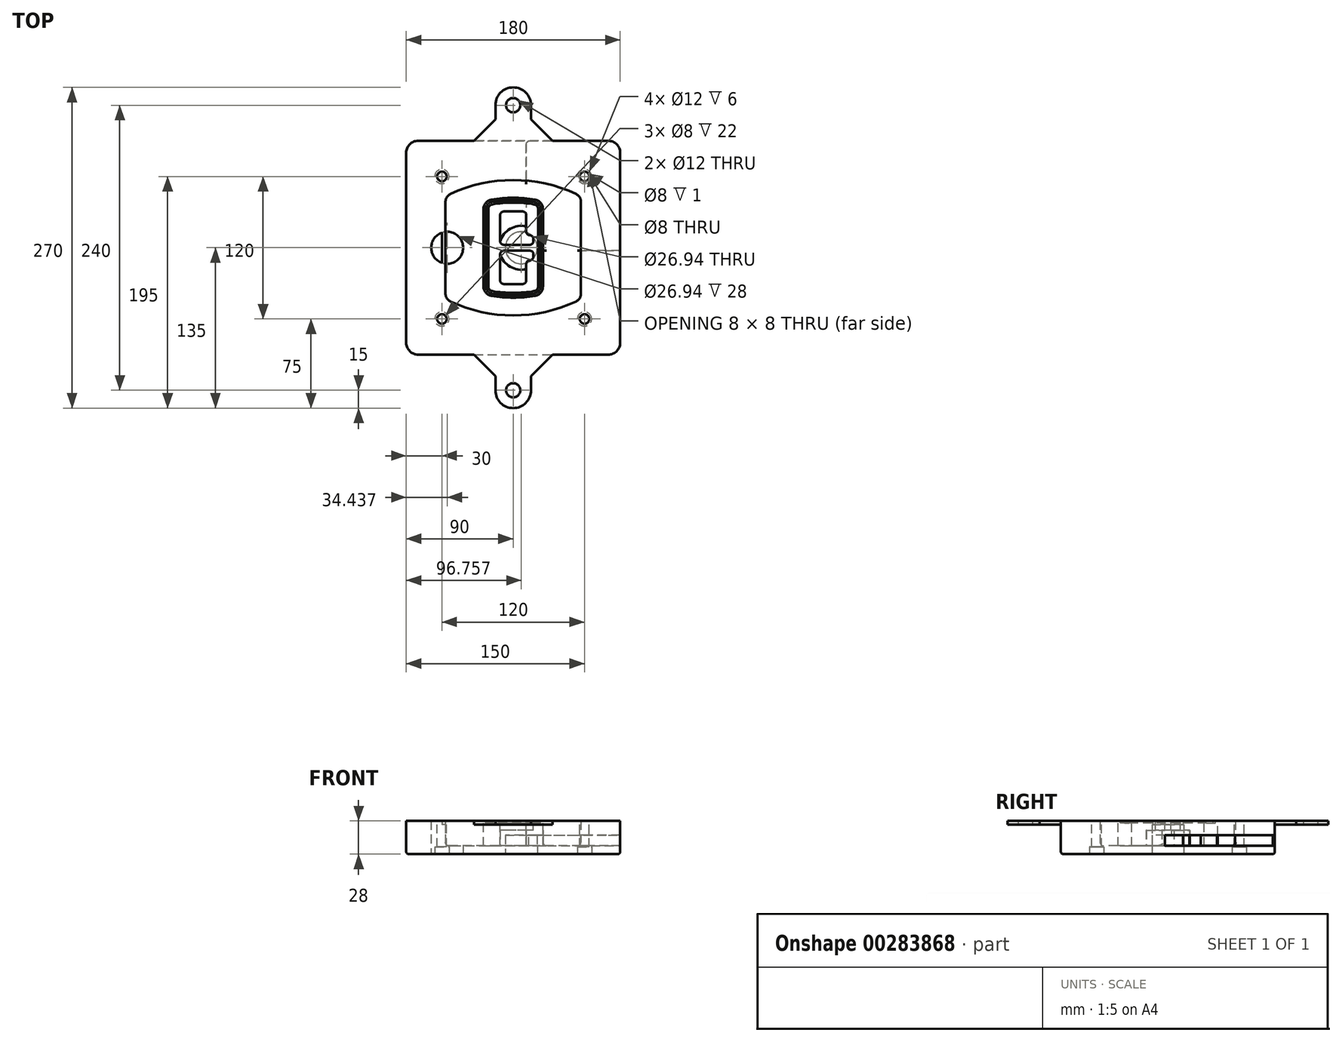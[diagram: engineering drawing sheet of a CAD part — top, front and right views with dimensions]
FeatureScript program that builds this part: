
annotation { "Feature Type Name" : "Feature", "Feature Type Description" : "" }
export const myFeature = defineFeature(function(context is Context, id is Id, definition is map)
    precondition{}
    {
        {
            var Q0;
            Q0=qCreatedBy(makeId("Top.planeOp"),FACE);
            var sketch = newSketch(context, id + "F0", { "sketchPlane" : qUnion([Q0])});
            skPoint(sketch, "E0.rect.middle", {"position": v(0, 0) * mm});
            skLineSegment(sketch, "E1.bottom", {"start": v(-80, -90) * mm, "end": v(80, -90) * mm});
            skLineSegment(sketch, "E1.top", {"start": v(-80, 90) * mm, "end": v(80, 90) * mm});
            skLineSegment(sketch, "E1.left", {"start": v(-90, -80) * mm, "end": v(-90, 80) * mm});
            skLineSegment(sketch, "E1.right", {"start": v(90, -80) * mm, "end": v(90, 80) * mm});
            skLineSegment(sketch, "E2", {"start": v(-90, 90) * mm, "end": v(90, -90) * mm, "construction": true});
            skLineSegment(sketch, "E3", {"start": v(90, 90) * mm, "end": v(-90, -90) * mm, "construction": true});
            skCircle(sketch, "E4", {"center": v(-60, 60) * mm, "radius": 4 * mm});
            skCircle(sketch, "E5", {"center": v(60, 60) * mm, "radius": 4 * mm});
            skCircle(sketch, "E6", {"center": v(60, -60) * mm, "radius": 4 * mm});
            skCircle(sketch, "E7", {"center": v(-60, -60) * mm, "radius": 4 * mm});
            skLineSegment(sketch, "E8", {"start": v(-60, 60) * mm, "end": v(60, 60) * mm, "construction": true});
            skLineSegment(sketch, "E9", {"start": v(60, 60) * mm, "end": v(60, -60) * mm, "construction": true});
            skLineSegment(sketch, "E10", {"start": v(60, -60) * mm, "end": v(-60, -60) * mm, "construction": true});
            skLineSegment(sketch, "E11", {"start": v(-60, -60) * mm, "end": v(-60, 60) * mm, "construction": true});
            skLineSegment(sketch, "E12", {"start": v(-60, 38.83) * mm, "end": v(-60, -38.83) * mm});
            skLineSegment(sketch, "E13", {"start": v(60, 38.83) * mm, "end": v(60, -38.83) * mm});
            skArc(sketch, "E14", {"start": v(54.26, 47.88) * mm, "mid": v(0, 60) * mm, "end": v(-54.26, 47.88) * mm});
            skArc(sketch, "E15", {"start": v(-54.26, -47.88) * mm, "mid": v(0, -60) * mm, "end": v(54.26, -47.88) * mm});
            skLineSegment(sketch, "E16", {"start": v(-60, 0) * mm, "end": v(60, 0) * mm, "construction": true});
            skPoint(sketch, "E17.visualSharp", {"position": v(-60, -45) * mm});
            skArc(sketch, "E17.filletArc", {"start": v(-60, -38.83) * mm, "mid": v(-58.44, -44.2) * mm, "end": v(-54.26, -47.88) * mm});
            skPoint(sketch, "E18.visualSharp", {"position": v(-60, 45) * mm});
            skArc(sketch, "E18.filletArc", {"start": v(-54.26, 47.88) * mm, "mid": v(-58.44, 44.2) * mm, "end": v(-60, 38.83) * mm});
            skPoint(sketch, "E19.visualSharp", {"position": v(60, 45) * mm});
            skArc(sketch, "E19.filletArc", {"start": v(60, 38.83) * mm, "mid": v(58.44, 44.2) * mm, "end": v(54.26, 47.88) * mm});
            skPoint(sketch, "E20.visualSharp", {"position": v(60, -45) * mm});
            skArc(sketch, "E20.filletArc", {"start": v(54.26, -47.88) * mm, "mid": v(58.44, -44.2) * mm, "end": v(60, -38.83) * mm});
            skPoint(sketch, "E21.visualSharp", {"position": v(-90, 90) * mm});
            skArc(sketch, "E21.filletArc", {"start": v(-80, 90) * mm, "mid": v(-87.07, 87.07) * mm, "end": v(-90, 80) * mm});
            skPoint(sketch, "E22.visualSharp", {"position": v(90, 90) * mm});
            skArc(sketch, "E22.filletArc", {"start": v(90, 80) * mm, "mid": v(87.07, 87.07) * mm, "end": v(80, 90) * mm});
            skPoint(sketch, "E23.visualSharp", {"position": v(90, -90) * mm});
            skArc(sketch, "E23.filletArc", {"start": v(80, -90) * mm, "mid": v(87.07, -87.07) * mm, "end": v(90, -80) * mm});
            skPoint(sketch, "E24.visualSharp", {"position": v(-90, -90) * mm});
            skArc(sketch, "E24.filletArc", {"start": v(-90, -80) * mm, "mid": v(-87.07, -87.07) * mm, "end": v(-80, -90) * mm});
            skArc(sketch, "E25.0", {"start": v(57, 38.83) * mm, "mid": v(55.9, 42.58) * mm, "end": v(52.98, 45.17) * mm});
            skLineSegment(sketch, "E25.1", {"start": v(57, 38.83) * mm, "end": v(57, -38.83) * mm});
            skArc(sketch, "E25.2", {"start": v(52.98, -45.17) * mm, "mid": v(55.9, -42.58) * mm, "end": v(57, -38.83) * mm});
            skArc(sketch, "E25.3", {"start": v(-52.98, -45.17) * mm, "mid": v(0, -57) * mm, "end": v(52.98, -45.17) * mm});
            skArc(sketch, "E25.4", {"start": v(-57, -38.83) * mm, "mid": v(-55.9, -42.58) * mm, "end": v(-52.98, -45.17) * mm});
            skArc(sketch, "E25.5", {"start": v(52.98, 45.17) * mm, "mid": v(0, 57) * mm, "end": v(-52.98, 45.17) * mm});
            skLineSegment(sketch, "E25.6", {"start": v(-57, 38.83) * mm, "end": v(-57, -38.83) * mm});
            skArc(sketch, "E25.7", {"start": v(-52.98, 45.17) * mm, "mid": v(-55.9, 42.58) * mm, "end": v(-57, 38.83) * mm});
            skArc(sketch, "E26.0", {"start": v(-55.96, 51.5) * mm, "mid": v(-61.82, 46.33) * mm, "end": v(-64, 38.83) * mm});
            skArc(sketch, "E26.1", {"start": v(55.96, 51.5) * mm, "mid": v(0, 64) * mm, "end": v(-55.96, 51.5) * mm});
            skArc(sketch, "E26.2", {"start": v(64, 38.83) * mm, "mid": v(61.82, 46.33) * mm, "end": v(55.96, 51.5) * mm});
            skLineSegment(sketch, "E26.3", {"start": v(64, 38.83) * mm, "end": v(64, -38.83) * mm});
            skArc(sketch, "E26.4", {"start": v(55.96, -51.5) * mm, "mid": v(61.82, -46.33) * mm, "end": v(64, -38.83) * mm});
            skLineSegment(sketch, "E26.5", {"start": v(-64, 38.83) * mm, "end": v(-64, -38.83) * mm});
            skArc(sketch, "E26.6", {"start": v(-55.96, -51.5) * mm, "mid": v(0, -64) * mm, "end": v(55.96, -51.5) * mm});
            skArc(sketch, "E26.7", {"start": v(-64, -38.83) * mm, "mid": v(-61.82, -46.33) * mm, "end": v(-55.96, -51.5) * mm});
            skSolve(sketch);
        }
        {
            var Q0;
            Q0=makeQuery(id+"F0.imprint","IMPRINT",FACE,{"disambiguationData":[TD([[makeQuery(id+"F0.imprint","IMPRINT",EDGE,{"derivedFrom":sQuery(id+"F0.wireOp",EDGE,"E1.bottom")}),1.0]])]});
            var Q1;
            Q1=makeQuery(id+"F0.imprint","IMPRINT",FACE,{"disambiguationData":[TD([[makeQuery(id+"F0.imprint","IMPRINT",EDGE,{"derivedFrom":sQuery(id+"F0.wireOp",EDGE,"E12")}),1.0]])]});
            var Q2;
            Q2=makeQuery(id+"F0.imprint","IMPRINT",FACE,{"disambiguationData":[TD([[makeQuery(id+"F0.imprint","IMPRINT",EDGE,{"derivedFrom":sQuery(id+"F0.wireOp",EDGE,"E25.0")}),1.0]])]});
            var Q3;
            Q3=makeQuery(id+"F0.imprint","IMPRINT",FACE,{"disambiguationData":[TD([[makeQuery(id+"F0.imprint","IMPRINT",EDGE,{"derivedFrom":sQuery(id+"F0.wireOp",EDGE,"E12")}),-1.0]])]});
            extrude(context, id + "F1", {"entities" : qUnion([Q0, Q1, Q2, Q3]), "oppositeDirection" : true, "depth" : 25 * mm});
        }
        {
            var Q0;
            Q0=makeQuery(id+"F0.imprint","IMPRINT",FACE,{"disambiguationData":[TD([[makeQuery(id+"F0.imprint","IMPRINT",EDGE,{"derivedFrom":sQuery(id+"F0.wireOp",EDGE,"E12")}),1.0]])]});
            extrude(context, id + "F2", {"entities" : qUnion([Q0]), "operationType" : NewBodyOperationType.ADD, "depth" : 3 * mm});
        }
        {
            var Q0;
            Q0=makeQuery(id+"F0.imprint","IMPRINT",FACE,{"disambiguationData":[TD([[makeQuery(id+"F0.imprint","IMPRINT",EDGE,{"derivedFrom":sQuery(id+"F0.wireOp",EDGE,"E25.0")}),1.0]])]});
            extrude(context, id + "F3", {"entities" : qUnion([Q0]), "operationType" : NewBodyOperationType.REMOVE, "oppositeDirection" : true, "depth" : 18 * mm});
        }
        {
            var Q0;
            Q0=makeQuery(id+"F2.opExtrude","CAP_FACE",FACE,{"disambiguationData":[OSD([sQuery(id+"F0.wireOp",EDGE,"E12"),sQuery(id+"F0.wireOp",EDGE,"E13"),sQuery(id+"F0.wireOp",EDGE,"E14"),sQuery(id+"F0.wireOp",EDGE,"E15"),sQuery(id+"F0.wireOp",EDGE,"E17.filletArc"),sQuery(id+"F0.wireOp",EDGE,"E18.filletArc"),sQuery(id+"F0.wireOp",EDGE,"E19.filletArc"),sQuery(id+"F0.wireOp",EDGE,"E20.filletArc"),sQuery(id+"F0.wireOp",EDGE,"E25.0"),sQuery(id+"F0.wireOp",EDGE,"E25.1"),sQuery(id+"F0.wireOp",EDGE,"E25.2"),sQuery(id+"F0.wireOp",EDGE,"E25.3"),sQuery(id+"F0.wireOp",EDGE,"E25.4"),sQuery(id+"F0.wireOp",EDGE,"E25.5"),sQuery(id+"F0.wireOp",EDGE,"E25.6"),sQuery(id+"F0.wireOp",EDGE,"E25.7")])],"isStart":false});
            var sketch = newSketch(context, id + "F4", { "sketchPlane" : qUnion([Q0])});
            skArc(sketch, "E27.0", {"start": v(-18.34, -40.45) * mm, "mid": v(0, -42) * mm, "end": v(18.34, -40.45) * mm});
            skArc(sketch, "E28.0", {"start": v(18.34, 40.45) * mm, "mid": v(0, 42) * mm, "end": v(-18.34, 40.45) * mm});
            skLineSegment(sketch, "E29", {"start": v(-25, 32.57) * mm, "end": v(-25, -32.57) * mm});
            skLineSegment(sketch, "E30", {"start": v(25, 32.57) * mm, "end": v(25, -32.57) * mm});
            skLineSegment(sketch, "E31", {"start": v(-25, 39.1) * mm, "end": v(25, 39.1) * mm, "construction": true});
            skLineSegment(sketch, "E32", {"start": v(-25, -39.1) * mm, "end": v(25, -39.1) * mm, "construction": true});
            skPoint(sketch, "E33.visualSharp", {"position": v(-25, 39.1) * mm});
            skArc(sketch, "E33.filletArc", {"start": v(-18.34, 40.45) * mm, "mid": v(-23.11, 37.73) * mm, "end": v(-25, 32.57) * mm});
            skPoint(sketch, "E34.visualSharp", {"position": v(25, 39.1) * mm});
            skArc(sketch, "E34.filletArc", {"start": v(25, 32.57) * mm, "mid": v(23.11, 37.73) * mm, "end": v(18.34, 40.45) * mm});
            skPoint(sketch, "E35.visualSharp", {"position": v(25, -39.1) * mm});
            skArc(sketch, "E35.filletArc", {"start": v(18.34, -40.45) * mm, "mid": v(23.11, -37.73) * mm, "end": v(25, -32.57) * mm});
            skPoint(sketch, "E36.visualSharp", {"position": v(-25, -39.1) * mm});
            skArc(sketch, "E36.filletArc", {"start": v(-25, -32.57) * mm, "mid": v(-23.11, -37.73) * mm, "end": v(-18.34, -40.45) * mm});
            skArc(sketch, "E37.0", {"start": v(52.98, 45.17) * mm, "mid": v(0, 57) * mm, "end": v(-52.98, 45.17) * mm});
            skArc(sketch, "E37.1", {"start": v(-52.98, 45.17) * mm, "mid": v(-55.9, 42.58) * mm, "end": v(-57, 38.83) * mm});
            skLineSegment(sketch, "E37.2", {"start": v(-57, 38.83) * mm, "end": v(-57, -38.83) * mm});
            skArc(sketch, "E37.3", {"start": v(-57, -38.83) * mm, "mid": v(-55.9, -42.58) * mm, "end": v(-52.98, -45.17) * mm});
            skArc(sketch, "E37.4", {"start": v(-52.98, -45.17) * mm, "mid": v(0, -57) * mm, "end": v(52.98, -45.17) * mm});
            skArc(sketch, "E37.5", {"start": v(52.98, -45.17) * mm, "mid": v(55.9, -42.58) * mm, "end": v(57, -38.83) * mm});
            skLineSegment(sketch, "E37.6", {"start": v(57, 38.83) * mm, "end": v(57, -38.83) * mm});
            skArc(sketch, "E37.7", {"start": v(57, 38.83) * mm, "mid": v(55.9, 42.58) * mm, "end": v(52.98, 45.17) * mm});
            skLineSegment(sketch, "E38.0", {"start": v(23, 32.57) * mm, "end": v(23, -32.57) * mm});
            skArc(sketch, "E38.1", {"start": v(18, -38.48) * mm, "mid": v(21.58, -36.44) * mm, "end": v(23, -32.57) * mm});
            skArc(sketch, "E38.2", {"start": v(-18, -38.48) * mm, "mid": v(0, -40) * mm, "end": v(18, -38.48) * mm});
            skArc(sketch, "E38.3", {"start": v(-23, -32.57) * mm, "mid": v(-21.58, -36.44) * mm, "end": v(-18, -38.48) * mm});
            skLineSegment(sketch, "E38.4", {"start": v(-23, 32.57) * mm, "end": v(-23, -32.57) * mm});
            skArc(sketch, "E38.5", {"start": v(23, 32.57) * mm, "mid": v(21.58, 36.44) * mm, "end": v(18, 38.48) * mm});
            skArc(sketch, "E38.6", {"start": v(-18, 38.48) * mm, "mid": v(-21.58, 36.44) * mm, "end": v(-23, 32.57) * mm});
            skArc(sketch, "E38.7", {"start": v(18, 38.48) * mm, "mid": v(0, 40) * mm, "end": v(-18, 38.48) * mm});
            skArc(sketch, "E39.0", {"start": v(21, 32.57) * mm, "mid": v(20.06, 35.15) * mm, "end": v(17.67, 36.5) * mm});
            skLineSegment(sketch, "E39.1", {"start": v(21, 32.57) * mm, "end": v(21, -32.57) * mm});
            skArc(sketch, "E39.2", {"start": v(17.67, -36.5) * mm, "mid": v(20.06, -35.15) * mm, "end": v(21, -32.57) * mm});
            skArc(sketch, "E39.3", {"start": v(-17.67, -36.5) * mm, "mid": v(0, -38) * mm, "end": v(17.67, -36.5) * mm});
            skArc(sketch, "E39.4", {"start": v(-21, -32.57) * mm, "mid": v(-20.06, -35.15) * mm, "end": v(-17.67, -36.5) * mm});
            skArc(sketch, "E39.5", {"start": v(17.67, 36.5) * mm, "mid": v(0, 38) * mm, "end": v(-17.67, 36.5) * mm});
            skLineSegment(sketch, "E39.6", {"start": v(-21, 32.57) * mm, "end": v(-21, -32.57) * mm});
            skArc(sketch, "E39.7", {"start": v(-17.67, 36.5) * mm, "mid": v(-20.06, 35.15) * mm, "end": v(-21, 32.57) * mm});
            skLineSegment(sketch, "E40", {"start": v(-25, 0) * mm, "end": v(25, 0) * mm, "construction": true});
            skLineSegment(sketch, "E41", {"start": v(-11, 5.5) * mm, "end": v(-11, 27.5) * mm});
            skLineSegment(sketch, "E42", {"start": v(-8, 30.5) * mm, "end": v(8, 30.5) * mm});
            skLineSegment(sketch, "E43", {"start": v(11, 27.5) * mm, "end": v(11, 13.5) * mm});
            skLineSegment(sketch, "E44", {"start": v(14, 10.5) * mm, "end": v(14, 10.5) * mm});
            skLineSegment(sketch, "E45", {"start": v(17, 7.5) * mm, "end": v(17, 5.5) * mm});
            skLineSegment(sketch, "E46", {"start": v(14, 2.5) * mm, "end": v(-8, 2.5) * mm});
            skPoint(sketch, "E47.visualSharp", {"position": v(-11, 30.5) * mm});
            skArc(sketch, "E47.filletArc", {"start": v(-8, 30.5) * mm, "mid": v(-10.12, 29.62) * mm, "end": v(-11, 27.5) * mm});
            skPoint(sketch, "E48.visualSharp", {"position": v(11, 30.5) * mm});
            skArc(sketch, "E48.filletArc", {"start": v(11, 27.5) * mm, "mid": v(10.12, 29.62) * mm, "end": v(8, 30.5) * mm});
            skPoint(sketch, "E49.visualSharp", {"position": v(11, 10.5) * mm});
            skArc(sketch, "E49.filletArc", {"start": v(11, 13.5) * mm, "mid": v(11.88, 11.38) * mm, "end": v(14, 10.5) * mm});
            skPoint(sketch, "E50.visualSharp", {"position": v(17, 10.5) * mm});
            skArc(sketch, "E50.filletArc", {"start": v(17, 7.5) * mm, "mid": v(16.12, 9.62) * mm, "end": v(14, 10.5) * mm});
            skPoint(sketch, "E51.visualSharp", {"position": v(17, 2.5) * mm});
            skArc(sketch, "E51.filletArc", {"start": v(14, 2.5) * mm, "mid": v(16.12, 3.38) * mm, "end": v(17, 5.5) * mm});
            skPoint(sketch, "E52.visualSharp", {"position": v(-11, 2.5) * mm});
            skArc(sketch, "E52.filletArc", {"start": v(-11, 5.5) * mm, "mid": v(-10.12, 3.38) * mm, "end": v(-8, 2.5) * mm});
            skLineSegment(sketch, "E53.0.MirrorCS", {"start": v(14, -2.5) * mm, "end": v(-8, -2.5) * mm});
            skArc(sketch, "E54.0.MirrorCS", {"start": v(-11, -5.5) * mm, "mid": v(-10.12, -3.38) * mm, "end": v(-8, -2.5) * mm});
            skLineSegment(sketch, "E55.0.MirrorCS", {"start": v(-11, -5.5) * mm, "end": v(-11, -27.5) * mm});
            skArc(sketch, "E56.0.MirrorCS", {"start": v(-8, -30.5) * mm, "mid": v(-10.12, -29.62) * mm, "end": v(-11, -27.5) * mm});
            skLineSegment(sketch, "E57.0.MirrorCS", {"start": v(-8, -30.5) * mm, "end": v(8, -30.5) * mm});
            skArc(sketch, "E58.0.MirrorCS", {"start": v(11, -27.5) * mm, "mid": v(10.12, -29.62) * mm, "end": v(8, -30.5) * mm});
            skLineSegment(sketch, "E59.0.MirrorCS", {"start": v(11, -27.5) * mm, "end": v(11, -13.5) * mm});
            skArc(sketch, "E60.0.MirrorCS", {"start": v(11, -13.5) * mm, "mid": v(11.88, -11.38) * mm, "end": v(14, -10.5) * mm});
            skArc(sketch, "E61.0.MirrorCS", {"start": v(17, -7.5) * mm, "mid": v(16.12, -9.62) * mm, "end": v(14, -10.5) * mm});
            skLineSegment(sketch, "E62.0.MirrorCS", {"start": v(17, -7.5) * mm, "end": v(17, -5.5) * mm});
            skArc(sketch, "E63.0.MirrorCS", {"start": v(14, -2.5) * mm, "mid": v(16.12, -3.38) * mm, "end": v(17, -5.5) * mm});
            skSolve(sketch);
        }
        {
            var Q0;
            Q0=makeQuery(id+"F4.imprint","IMPRINT",FACE,{"disambiguationData":[TD([[makeQuery(id+"F4.imprint","IMPRINT",EDGE,{"derivedFrom":sQuery(id+"F4.wireOp",EDGE,"E27.0")}),1.0]])]});
            var Q1;
            Q1=makeQuery(id+"F4.imprint","IMPRINT",FACE,{"disambiguationData":[TD([[makeQuery(id+"F4.imprint","IMPRINT",EDGE,{"derivedFrom":sQuery(id+"F4.wireOp",EDGE,"E38.0")}),-1.0]])]});
            var Q2;
            Q2=makeQuery(id+"F4.imprint","IMPRINT",FACE,{"disambiguationData":[TD([[makeQuery(id+"F4.imprint","IMPRINT",EDGE,{"derivedFrom":sQuery(id+"F4.wireOp",EDGE,"E39.0")}),1.0]])]});
            extrude(context, id + "F5", {"entities" : qUnion([Q0, Q1, Q2]), "operationType" : NewBodyOperationType.ADD, "endBound" : BoundingType.UP_TO_NEXT, "oppositeDirection" : true, "depth" : 25 * mm});
        }
        {
            var Q0;
            Q0=makeQuery(id+"F4.imprint","IMPRINT",FACE,{"disambiguationData":[TD([[makeQuery(id+"F4.imprint","IMPRINT",EDGE,{"derivedFrom":sQuery(id+"F4.wireOp",EDGE,"E38.0")}),-1.0]])]});
            extrude(context, id + "F6", {"entities" : qUnion([Q0]), "operationType" : NewBodyOperationType.REMOVE, "oppositeDirection" : true, "depth" : 2 * mm});
        }
        {
            var Q0;
            Q0=makeQuery(id+"F1.opExtrude","CAP_FACE",FACE,{"disambiguationData":[OSD([sQuery(id+"F0.wireOp",EDGE,"E1.bottom"),sQuery(id+"F0.wireOp",EDGE,"E1.top"),sQuery(id+"F0.wireOp",EDGE,"E1.left"),sQuery(id+"F0.wireOp",EDGE,"E1.right"),sQuery(id+"F0.wireOp",EDGE,"E4"),sQuery(id+"F0.wireOp",EDGE,"E5"),sQuery(id+"F0.wireOp",EDGE,"E6"),sQuery(id+"F0.wireOp",EDGE,"E7"),sQuery(id+"F0.wireOp",EDGE,"E21.filletArc"),sQuery(id+"F0.wireOp",EDGE,"E22.filletArc"),sQuery(id+"F0.wireOp",EDGE,"E23.filletArc"),sQuery(id+"F0.wireOp",EDGE,"E24.filletArc")])],"isStart":false});
            var sketch = newSketch(context, id + "F7", { "sketchPlane" : qUnion([Q0])});
            skCircle(sketch, "E64", {"center": v(6.76, 0) * mm, "radius": 13.47 * mm});
            skCircle(sketch, "E65", {"center": v(-55.56, 0) * mm, "radius": 13.47 * mm});
            skLineSegment(sketch, "E66", {"start": v(90, 0) * mm, "end": v(-90, 0) * mm});
            skCircle(sketch, "E67", {"center": v(6.76, 0) * mm, "radius": 18.47 * mm});
            skCircle(sketch, "E68", {"center": v(60, -60) * mm, "radius": 6 * mm});
            skCircle(sketch, "E69", {"center": v(-60, -60) * mm, "radius": 6 * mm});
            skCircle(sketch, "E70", {"center": v(-60, 60) * mm, "radius": 6 * mm});
            skCircle(sketch, "E71", {"center": v(60, 60) * mm, "radius": 6 * mm});
            skSolve(sketch);
        }
        {
            var Q0;
            {var subQ1=sQuery(id+"F7.wireOp",EDGE,"E66");var subQ4=sQuery(id+"F7.wireOp",EDGE,"E64");var subQ6=makeQuery(id+"F7.imprint","INTERSECT",VERTEX,{"disambiguationData":[OD(0.0)],"derivedFrom":[subQ4,subQ1]});Q0=makeQuery(id+"F7.imprint","IMPRINT",FACE,{"disambiguationData":[TD([[makeQuery(id+"F7.imprint","IMPRINT",EDGE,{"disambiguationData":[TD([[subQ6,-1.0]])],"derivedFrom":subQ4}),-1.0]])]});}
            var Q1;
            {var subQ0=sQuery(id+"F7.wireOp",EDGE,"E66");var subQ1=sQuery(id+"F7.wireOp",EDGE,"E64");var subQ3=makeQuery(id+"F7.imprint","INTERSECT",VERTEX,{"disambiguationData":[OD(0.0)],"derivedFrom":[subQ1,subQ0]});Q1=makeQuery(id+"F7.imprint","IMPRINT",FACE,{"disambiguationData":[TD([[makeQuery(id+"F7.imprint","IMPRINT",EDGE,{"disambiguationData":[TD([[subQ3,-1.0]])],"derivedFrom":subQ1}),1.0]])]});}
            var Q2;
            {var subQ0=sQuery(id+"F7.wireOp",EDGE,"E66");var subQ1=sQuery(id+"F7.wireOp",EDGE,"E64");var subQ3=makeQuery(id+"F7.imprint","INTERSECT",VERTEX,{"disambiguationData":[OD(0.0)],"derivedFrom":[subQ1,subQ0]});Q2=makeQuery(id+"F7.imprint","IMPRINT",FACE,{"disambiguationData":[TD([[makeQuery(id+"F7.imprint","IMPRINT",EDGE,{"disambiguationData":[TD([[subQ3,1.0]])],"derivedFrom":subQ1}),1.0]])]});}
            var Q3;
            {var subQ1=sQuery(id+"F7.wireOp",EDGE,"E66");var subQ4=sQuery(id+"F7.wireOp",EDGE,"E64");var subQ6=makeQuery(id+"F7.imprint","INTERSECT",VERTEX,{"disambiguationData":[OD(0.0)],"derivedFrom":[subQ4,subQ1]});Q3=makeQuery(id+"F7.imprint","IMPRINT",FACE,{"disambiguationData":[TD([[makeQuery(id+"F7.imprint","IMPRINT",EDGE,{"disambiguationData":[TD([[subQ6,1.0]])],"derivedFrom":subQ4}),-1.0]])]});}
            extrude(context, id + "F8", {"entities" : qUnion([Q0, Q1, Q2, Q3]), "operationType" : NewBodyOperationType.ADD, "oppositeDirection" : true, "depth" : 20 * mm});
        }
        {
            var Q0;
            {var subQ0=sQuery(id+"F7.wireOp",EDGE,"E66");var subQ1=sQuery(id+"F7.wireOp",EDGE,"E64");var subQ3=makeQuery(id+"F7.imprint","INTERSECT",VERTEX,{"disambiguationData":[OD(0.0)],"derivedFrom":[subQ1,subQ0]});Q0=makeQuery(id+"F7.imprint","IMPRINT",FACE,{"disambiguationData":[TD([[makeQuery(id+"F7.imprint","IMPRINT",EDGE,{"disambiguationData":[TD([[subQ3,-1.0]])],"derivedFrom":subQ1}),1.0]])]});}
            var Q1;
            {var subQ0=sQuery(id+"F7.wireOp",EDGE,"E66");var subQ1=sQuery(id+"F7.wireOp",EDGE,"E64");var subQ3=makeQuery(id+"F7.imprint","INTERSECT",VERTEX,{"disambiguationData":[OD(0.0)],"derivedFrom":[subQ1,subQ0]});Q1=makeQuery(id+"F7.imprint","IMPRINT",FACE,{"disambiguationData":[TD([[makeQuery(id+"F7.imprint","IMPRINT",EDGE,{"disambiguationData":[TD([[subQ3,1.0]])],"derivedFrom":subQ1}),1.0]])]});}
            extrude(context, id + "F9", {"entities" : qUnion([Q0, Q1]), "operationType" : NewBodyOperationType.REMOVE, "oppositeDirection" : true, "depth" : 16 * mm});
        }
        {
            var Q0;
            {var subQ0=sQuery(id+"F7.wireOp",EDGE,"E66");var subQ1=sQuery(id+"F7.wireOp",EDGE,"E65");var subQ3=makeQuery(id+"F7.imprint","INTERSECT",VERTEX,{"disambiguationData":[OD(0.0)],"derivedFrom":[subQ1,subQ0]});Q0=makeQuery(id+"F7.imprint","IMPRINT",FACE,{"disambiguationData":[TD([[makeQuery(id+"F7.imprint","IMPRINT",EDGE,{"disambiguationData":[TD([[subQ3,-1.0]])],"derivedFrom":subQ1}),1.0]])]});}
            var Q1;
            {var subQ0=sQuery(id+"F7.wireOp",EDGE,"E66");var subQ1=sQuery(id+"F7.wireOp",EDGE,"E65");var subQ3=makeQuery(id+"F7.imprint","INTERSECT",VERTEX,{"disambiguationData":[OD(0.0)],"derivedFrom":[subQ1,subQ0]});Q1=makeQuery(id+"F7.imprint","IMPRINT",FACE,{"disambiguationData":[TD([[makeQuery(id+"F7.imprint","IMPRINT",EDGE,{"disambiguationData":[TD([[subQ3,1.0]])],"derivedFrom":subQ1}),1.0]])]});}
            extrude(context, id + "F10", {"entities" : qUnion([Q0, Q1]), "operationType" : NewBodyOperationType.REMOVE, "oppositeDirection" : true, "depth" : 25 * mm});
        }
        {
            var Q0;
            Q0=makeQuery(id+"F7.imprint","IMPRINT",FACE,{"disambiguationData":[TD([[makeQuery(id+"F7.imprint","IMPRINT",EDGE,{"derivedFrom":sQuery(id+"F7.wireOp",EDGE,"E68")}),1.0]])]});
            var Q1;
            Q1=makeQuery(id+"F7.imprint","IMPRINT",FACE,{"disambiguationData":[TD([[makeQuery(id+"F7.imprint","IMPRINT",EDGE,{"derivedFrom":makeQuery(id+"F1.opExtrude","CAP_EDGE",EDGE,{"disambiguationData":[OSD([sQuery(id+"F0.wireOp",EDGE,"E5")])],"isStart":false})}),-1.0]])]});
            var Q2;
            Q2=makeQuery(id+"F7.imprint","IMPRINT",FACE,{"disambiguationData":[TD([[makeQuery(id+"F7.imprint","IMPRINT",EDGE,{"derivedFrom":sQuery(id+"F7.wireOp",EDGE,"E69")}),1.0]])]});
            var Q3;
            Q3=makeQuery(id+"F7.imprint","IMPRINT",FACE,{"disambiguationData":[TD([[makeQuery(id+"F7.imprint","IMPRINT",EDGE,{"derivedFrom":makeQuery(id+"F1.opExtrude","CAP_EDGE",EDGE,{"disambiguationData":[OSD([sQuery(id+"F0.wireOp",EDGE,"E4")])],"isStart":false})}),-1.0]])]});
            var Q4;
            Q4=makeQuery(id+"F7.imprint","IMPRINT",FACE,{"disambiguationData":[TD([[makeQuery(id+"F7.imprint","IMPRINT",EDGE,{"derivedFrom":sQuery(id+"F7.wireOp",EDGE,"E70")}),1.0]])]});
            var Q5;
            Q5=makeQuery(id+"F7.imprint","IMPRINT",FACE,{"disambiguationData":[TD([[makeQuery(id+"F7.imprint","IMPRINT",EDGE,{"derivedFrom":makeQuery(id+"F1.opExtrude","CAP_EDGE",EDGE,{"disambiguationData":[OSD([sQuery(id+"F0.wireOp",EDGE,"E7")])],"isStart":false})}),-1.0]])]});
            var Q6;
            Q6=makeQuery(id+"F7.imprint","IMPRINT",FACE,{"disambiguationData":[TD([[makeQuery(id+"F7.imprint","IMPRINT",EDGE,{"derivedFrom":sQuery(id+"F7.wireOp",EDGE,"E71")}),1.0]])]});
            var Q7;
            Q7=makeQuery(id+"F7.imprint","IMPRINT",FACE,{"disambiguationData":[TD([[makeQuery(id+"F7.imprint","IMPRINT",EDGE,{"derivedFrom":makeQuery(id+"F1.opExtrude","CAP_EDGE",EDGE,{"disambiguationData":[OSD([sQuery(id+"F0.wireOp",EDGE,"E6")])],"isStart":false})}),-1.0]])]});
            extrude(context, id + "F11", {"entities" : qUnion([Q0, Q1, Q2, Q3, Q4, Q5, Q6, Q7]), "operationType" : NewBodyOperationType.REMOVE, "oppositeDirection" : true, "depth" : 6 * mm});
        }
        {
            var Q0;
            Q0=makeQuery(id+"F9.boolean.opBoolean","COPY",FACE,{"derivedFrom":makeQuery(id+"F9.opExtrude","CAP_FACE",FACE,{"disambiguationData":[OSD([sQuery(id+"F7.wireOp",EDGE,"E64")])],"isStart":false})});
            var sketch = newSketch(context, id + "F12", { "sketchPlane" : qUnion([Q0])});
            skArc(sketch, "E72.0", {"start": v(11, -88.19) * mm, "mid": v(97.1, -83.6) * mm, "end": v(92.5, 2.5) * mm});
            skLineSegment(sketch, "E72.1", {"start": v(11, -17.97) * mm, "end": v(11, -17.97) * mm});
            skLineSegment(sketch, "E73", {"start": v(92.5, -105.13) * mm, "end": v(102.3, -105.13) * mm});
            skLineSegment(sketch, "E74.0", {"start": v(92.5, 2.5) * mm, "end": v(14, 2.5) * mm});
            skArc(sketch, "E74.1", {"start": v(14, 2.5) * mm, "mid": v(16.12, 3.38) * mm, "end": v(17, 5.5) * mm});
            skLineSegment(sketch, "E74.2", {"start": v(17, 7.5) * mm, "end": v(17, 5.5) * mm});
            skArc(sketch, "E74.3", {"start": v(17, 7.5) * mm, "mid": v(16.12, 9.62) * mm, "end": v(14, 10.5) * mm});
            skArc(sketch, "E74.4", {"start": v(11, 13.5) * mm, "mid": v(11.88, 11.38) * mm, "end": v(14, 10.5) * mm});
            skLineSegment(sketch, "E74.5", {"start": v(11, 13.5) * mm, "end": v(11, -88.19) * mm});
            skLineSegment(sketch, "E74.7", {"start": v(92.5, -2.5) * mm, "end": v(14, -2.5) * mm});
            skArc(sketch, "E74.8", {"start": v(14, -2.5) * mm, "mid": v(16.12, -3.38) * mm, "end": v(17, -5.5) * mm});
            skLineSegment(sketch, "E74.9", {"start": v(17, -7.5) * mm, "end": v(17, -5.5) * mm});
            skArc(sketch, "E74.10", {"start": v(17, -7.5) * mm, "mid": v(16.12, -9.62) * mm, "end": v(14, -10.5) * mm});
            skArc(sketch, "E74.11", {"start": v(11, -13.5) * mm, "mid": v(11.88, -11.38) * mm, "end": v(14, -10.5) * mm});
            skLineSegment(sketch, "E74.12", {"start": v(11, -17.97) * mm, "end": v(11, -13.5) * mm});
            skPoint(sketch, "E75.orphan", {"position": v(11, -27.5) * mm});
            skPoint(sketch, "E76.orphan", {"position": v(-8, -2.5) * mm});
            skPoint(sketch, "E77.orphan", {"position": v(-8, 2.5) * mm});
            skPoint(sketch, "E78.orphan", {"position": v(11, 27.5) * mm});
            skSolve(sketch);
        }
        {
            var Q0;
            {var subQ7=sQuery(id+"F12.wireOp",EDGE,"E72.0");var subQ14=sQuery(id+"F12.wireOp",EDGE,"E72.1");var subQ16=sQuery(id+"F12.wireOp",EDGE,"E74.1");var subQ18=sQuery(id+"F12.wireOp",EDGE,"E74.8");Q0=qUnion([makeQuery(id+"F12.imprint","IMPRINT",FACE,{"disambiguationData":[TD([[makeQuery(id+"F12.imprint","IMPRINT",EDGE,{"derivedFrom":subQ7}),1.0]])]}),makeQuery(id+"F12.imprint","IMPRINT",FACE,{"disambiguationData":[TD([[makeQuery(id+"F12.imprint","IMPRINT",EDGE,{"derivedFrom":subQ14}),1.0]])]}),makeQuery(id+"F12.imprint","IMPRINT",FACE,{"disambiguationData":[TD([[makeQuery(id+"F12.imprint","IMPRINT",EDGE,{"derivedFrom":subQ16}),1.0]])]}),makeQuery(id+"F12.imprint","IMPRINT",FACE,{"disambiguationData":[TD([[makeQuery(id+"F12.imprint","IMPRINT",EDGE,{"derivedFrom":subQ18}),-1.0]])]})]);}
            var Q1;
            Q1=makeQuery(id+"F5.boolean.opBoolean","SPLIT",FACE,{"disambiguationData":[TD([makeQuery(id+"F5.opExtrude","SWEPT_FACE",FACE,{"disambiguationData":[OSD([sQuery(id+"F4.wireOp",EDGE,"E41")])]})])],"derivedFrom":makeQuery(id+"F3.boolean.opBoolean","COPY",FACE,{"derivedFrom":makeQuery(id+"F3.opExtrude","CAP_FACE",FACE,{"disambiguationData":[OSD([sQuery(id+"F0.wireOp",EDGE,"E25.0"),sQuery(id+"F0.wireOp",EDGE,"E25.1"),sQuery(id+"F0.wireOp",EDGE,"E25.2"),sQuery(id+"F0.wireOp",EDGE,"E25.3"),sQuery(id+"F0.wireOp",EDGE,"E25.4"),sQuery(id+"F0.wireOp",EDGE,"E25.5"),sQuery(id+"F0.wireOp",EDGE,"E25.6"),sQuery(id+"F0.wireOp",EDGE,"E25.7")])],"isStart":false})})});
            extrude(context, id + "F13", {"entities" : qUnion([Q0]), "operationType" : NewBodyOperationType.REMOVE, "endBound" : BoundingType.UP_TO_SURFACE, "endBoundEntityFace" : qUnion([Q1]), "depth" : 25 * mm});
        }
        {
            var Q0;
            Q0=makeQuery(id+"F3.boolean.opBoolean","COPY",EDGE,{"derivedFrom":makeQuery(id+"F3.opExtrude","CAP_EDGE",EDGE,{"disambiguationData":[OSD([sQuery(id+"F0.wireOp",EDGE,"E25.6")])],"isStart":false})});
            var Q1;
            Q1=makeQuery(id+"F8.boolean.opBoolean","INTERSECT",EDGE,{"derivedFrom":[makeQuery(id+"F5.opExtrude","SWEPT_FACE",FACE,{"disambiguationData":[OSD([sQuery(id+"F4.wireOp",EDGE,"E30")])]}),makeQuery(id+"F8.opExtrude","CAP_FACE",FACE,{"disambiguationData":[OSD([sQuery(id+"F7.wireOp",EDGE,"E67")])],"isStart":false})]});
            var Q2;
            Q2=makeQuery(id+"F8.boolean.opBoolean","INTERSECT",EDGE,{"disambiguationData":[OD(1.0)],"derivedFrom":[makeQuery(id+"F5.opExtrude","SWEPT_FACE",FACE,{"disambiguationData":[OSD([sQuery(id+"F4.wireOp",EDGE,"E30")])]}),makeQuery(id+"F8.opExtrude","SWEPT_FACE",FACE,{"disambiguationData":[OSD([sQuery(id+"F7.wireOp",EDGE,"E67")])]})]});
            var Q3;
            {var subQ0=makeQuery(id+"F3.boolean.opBoolean","COPY",FACE,{"derivedFrom":makeQuery(id+"F3.opExtrude","CAP_FACE",FACE,{"disambiguationData":[OSD([sQuery(id+"F0.wireOp",EDGE,"E25.0"),sQuery(id+"F0.wireOp",EDGE,"E25.1"),sQuery(id+"F0.wireOp",EDGE,"E25.2"),sQuery(id+"F0.wireOp",EDGE,"E25.3"),sQuery(id+"F0.wireOp",EDGE,"E25.4"),sQuery(id+"F0.wireOp",EDGE,"E25.5"),sQuery(id+"F0.wireOp",EDGE,"E25.6"),sQuery(id+"F0.wireOp",EDGE,"E25.7")])],"isStart":false})});var subQ1=sQuery(id+"F4.wireOp",EDGE,"E30");Q3=makeQuery(id+"F8.boolean.opBoolean","SPLIT",EDGE,{"disambiguationData":[TD([makeQuery(id+"F5.opExtrude","SWEPT_FACE",FACE,{"disambiguationData":[OSD([sQuery(id+"F4.wireOp",EDGE,"E35.filletArc")])]})])],"derivedFrom":makeQuery(id+"F5.opExtrude","TWEAK_EDGE",EDGE,{"derivedFrom":[subQ0,makeQuery(id+"F4.imprint","IMPRINT",EDGE,{"derivedFrom":subQ1})]})});}
            var Q4;
            {var subQ0=sQuery(id+"F0.wireOp",EDGE,"E25.0");var subQ1=sQuery(id+"F0.wireOp",EDGE,"E25.1");var subQ2=sQuery(id+"F0.wireOp",EDGE,"E25.2");var subQ3=sQuery(id+"F0.wireOp",EDGE,"E25.3");var subQ4=sQuery(id+"F0.wireOp",EDGE,"E25.4");var subQ5=sQuery(id+"F0.wireOp",EDGE,"E25.5");var subQ6=sQuery(id+"F0.wireOp",EDGE,"E25.6");var subQ7=sQuery(id+"F0.wireOp",EDGE,"E25.7");Q4=makeQuery(id+"F8.boolean.opBoolean","INTERSECT",EDGE,{"derivedFrom":[makeQuery(id+"F5.boolean.opBoolean","SPLIT",FACE,{"disambiguationData":[TD([makeQuery(id+"F2.opExtrude","SWEPT_FACE",FACE,{"disambiguationData":[OSD([subQ0])]})])],"derivedFrom":makeQuery(id+"F3.boolean.opBoolean","COPY",FACE,{"derivedFrom":makeQuery(id+"F3.opExtrude","CAP_FACE",FACE,{"disambiguationData":[OSD([subQ0,subQ1,subQ2,subQ3,subQ4,subQ5,subQ6,subQ7])],"isStart":false})})}),makeQuery(id+"F8.opExtrude","SWEPT_FACE",FACE,{"disambiguationData":[OSD([sQuery(id+"F7.wireOp",EDGE,"E67")])]})]});}
            var Q5;
            Q5=makeQuery(id+"F8.boolean.opBoolean","INTERSECT",EDGE,{"disambiguationData":[OD(0.0)],"derivedFrom":[makeQuery(id+"F5.opExtrude","SWEPT_FACE",FACE,{"disambiguationData":[OSD([sQuery(id+"F4.wireOp",EDGE,"E30")])]}),makeQuery(id+"F8.opExtrude","SWEPT_FACE",FACE,{"disambiguationData":[OSD([sQuery(id+"F7.wireOp",EDGE,"E67")])]})]});
            fillet(context, id + "F14", {"entities" : qUnion([Q0, Q1, Q2, Q3, Q4, Q5]), "radius" : 3 * mm, "tangentPropagation" : true, "allowEdgeOverflow" : false});
        }
        {
            var Q0;
            Q0=makeQuery(id+"F1.opExtrude","CAP_EDGE",EDGE,{"disambiguationData":[OSD([sQuery(id+"F0.wireOp",EDGE,"E1.bottom")])],"isStart":false});
            fillet(context, id + "F15", {"entities" : qUnion([Q0]), "radius" : 2 * mm, "tangentPropagation" : true, "allowEdgeOverflow" : false});
        }
        {
            var Q0;
            {var subQ0=sQuery(id+"F0.wireOp",EDGE,"E21.filletArc");var subQ1=sQuery(id+"F0.wireOp",EDGE,"E7");var subQ2=sQuery(id+"F0.wireOp",EDGE,"E6");var subQ3=sQuery(id+"F0.wireOp",EDGE,"E5");var subQ4=sQuery(id+"F0.wireOp",EDGE,"E4");var subQ5=sQuery(id+"F0.wireOp",EDGE,"E22.filletArc");var subQ6=sQuery(id+"F0.wireOp",EDGE,"E1.bottom");var subQ7=sQuery(id+"F0.wireOp",EDGE,"E1.right");var subQ8=sQuery(id+"F0.wireOp",EDGE,"E1.top");var subQ9=sQuery(id+"F0.wireOp",EDGE,"E1.left");var subQ10=sQuery(id+"F0.wireOp",EDGE,"E23.filletArc");var subQ11=sQuery(id+"F0.wireOp",EDGE,"E24.filletArc");Q0=makeQuery(id+"F2.boolean.opBoolean","SPLIT",FACE,{"disambiguationData":[TD([makeQuery(id+"F1.opExtrude","SWEPT_FACE",FACE,{"disambiguationData":[OSD([subQ6])]})])],"derivedFrom":makeQuery(id+"F1.opExtrude","CAP_FACE",FACE,{"disambiguationData":[OSD([subQ6,subQ8,subQ9,subQ7,subQ4,subQ3,subQ2,subQ1,subQ0,subQ5,subQ10,subQ11])],"isStart":true})});}
            var sketch = newSketch(context, id + "F16", { "sketchPlane" : qUnion([Q0])});
            skLineSegment(sketch, "E79.0", {"start": v(-80, 90) * mm, "end": v(-33, 90) * mm});
            skArc(sketch, "E79.1", {"start": v(-80, 90) * mm, "mid": v(-87.07, 87.07) * mm, "end": v(-90, 80) * mm});
            skLineSegment(sketch, "E79.2", {"start": v(-90, -80) * mm, "end": v(-90, 80) * mm});
            skCircle(sketch, "E79.3", {"center": v(-60, 60) * mm, "radius": 4 * mm});
            skArc(sketch, "E79.4", {"start": v(54.26, 47.88) * mm, "mid": v(0, 60) * mm, "end": v(-54.26, 47.88) * mm});
            skLineSegment(sketch, "E79.5", {"start": v(-60, 38.83) * mm, "end": v(-60, -38.83) * mm});
            skArc(sketch, "E79.6", {"start": v(-54.26, -47.88) * mm, "mid": v(0, -60) * mm, "end": v(54.26, -47.88) * mm});
            skArc(sketch, "E79.7", {"start": v(-60, -38.83) * mm, "mid": v(-58.44, -44.2) * mm, "end": v(-54.26, -47.88) * mm});
            skCircle(sketch, "E79.8", {"center": v(-60, -60) * mm, "radius": 4 * mm});
            skArc(sketch, "E79.9", {"start": v(-90, -80) * mm, "mid": v(-87.07, -87.07) * mm, "end": v(-80, -90) * mm});
            skLineSegment(sketch, "E79.10", {"start": v(-80, -90) * mm, "end": v(80, -90) * mm});
            skArc(sketch, "E79.11", {"start": v(80, -90) * mm, "mid": v(87.07, -87.07) * mm, "end": v(90, -80) * mm});
            skLineSegment(sketch, "E79.12", {"start": v(90, -80) * mm, "end": v(90, 80) * mm});
            skCircle(sketch, "E79.13", {"center": v(60, -60) * mm, "radius": 4 * mm});
            skArc(sketch, "E79.14", {"start": v(54.26, -47.88) * mm, "mid": v(58.44, -44.2) * mm, "end": v(60, -38.83) * mm});
            skLineSegment(sketch, "E79.15", {"start": v(60, 38.83) * mm, "end": v(60, -38.83) * mm});
            skArc(sketch, "E79.16", {"start": v(90, 80) * mm, "mid": v(87.07, 87.07) * mm, "end": v(80, 90) * mm});
            skArc(sketch, "E79.17", {"start": v(60, 38.83) * mm, "mid": v(58.44, 44.2) * mm, "end": v(54.26, 47.88) * mm});
            skCircle(sketch, "E79.18", {"center": v(60, 60) * mm, "radius": 4 * mm});
            skArc(sketch, "E79.19", {"start": v(-54.26, 47.88) * mm, "mid": v(-58.44, 44.2) * mm, "end": v(-60, 38.83) * mm});
            skPoint(sketch, "E80.end.orphan", {"position": v(0, 90) * mm});
            skLineSegment(sketch, "E81", {"start": v(0, 90) * mm, "end": v(0, 120) * mm, "construction": true});
            skLineSegment(sketch, "E82", {"start": v(-15, 108) * mm, "end": v(-15, 120) * mm});
            skArc(sketch, "E83", {"start": v(-15, 120) * mm, "mid": v(0, 135) * mm, "end": v(15, 120) * mm});
            skLineSegment(sketch, "E84", {"start": v(15, 120) * mm, "end": v(15, 108) * mm});
            skLineSegment(sketch, "E85", {"start": v(-15, 108) * mm, "end": v(-33, 90) * mm});
            skLineSegment(sketch, "E86", {"start": v(-33, 90) * mm, "end": v(-15, 108) * mm});
            skLineSegment(sketch, "E87", {"start": v(15, 108) * mm, "end": v(33, 90) * mm});
            skCircle(sketch, "E88", {"center": v(0, 120) * mm, "radius": 6 * mm});
            skLineSegment(sketch, "E89.trimOffspring", {"start": v(33, 90) * mm, "end": v(80, 90) * mm});
            skPoint(sketch, "E90.endSnap0", {"position": v(0, -90) * mm});
            skLineSegment(sketch, "E91", {"start": v(-90, 0) * mm, "end": v(90, 0) * mm, "construction": true});
            skArc(sketch, "E92.MirrorCS", {"start": v(-15, -120) * mm, "mid": v(0, -135) * mm, "end": v(15, -120) * mm});
            skLineSegment(sketch, "E93.MirrorCS", {"start": v(15, -120) * mm, "end": v(15, -108) * mm});
            skCircle(sketch, "E94.MirrorC", {"center": v(0, -120) * mm, "radius": 6 * mm});
            skLineSegment(sketch, "E95.MirrorCS", {"start": v(-33, -90) * mm, "end": v(-15, -108) * mm});
            skLineSegment(sketch, "E96.MirrorCS", {"start": v(15, -108) * mm, "end": v(33, -90) * mm});
            skLineSegment(sketch, "E97.MirrorCS", {"start": v(-15, -108) * mm, "end": v(-15, -120) * mm});
            skSolve(sketch);
        }
        {
            var Q0;
            Q0=makeQuery(id+"F16.imprint","IMPRINT",FACE,{"disambiguationData":[TD([[makeQuery(id+"F16.imprint","IMPRINT",EDGE,{"derivedFrom":sQuery(id+"F16.wireOp",EDGE,"E82")}),-1.0]])]});
            var Q1;
            {var subQ5=sQuery(id+"F16.wireOp",EDGE,"E79.0");Q1=makeQuery(id+"F16.imprint","IMPRINT",FACE,{"disambiguationData":[TD([[makeQuery(id+"F16.imprint","IMPRINT",EDGE,{"derivedFrom":subQ5}),-1.0]])]});}
            var Q2;
            Q2=makeQuery(id+"F16.imprint","IMPRINT",FACE,{"disambiguationData":[TD([[makeQuery(id+"F16.imprint","IMPRINT",EDGE,{"derivedFrom":sQuery(id+"F16.wireOp",EDGE,"E92.MirrorCS")}),1.0]])]});
            var Q3;
            Q3=makeQuery(id+"F2.opExtrude","CAP_FACE",FACE,{"disambiguationData":[OSD([sQuery(id+"F0.wireOp",EDGE,"E12"),sQuery(id+"F0.wireOp",EDGE,"E13"),sQuery(id+"F0.wireOp",EDGE,"E14"),sQuery(id+"F0.wireOp",EDGE,"E15"),sQuery(id+"F0.wireOp",EDGE,"E17.filletArc"),sQuery(id+"F0.wireOp",EDGE,"E18.filletArc"),sQuery(id+"F0.wireOp",EDGE,"E19.filletArc"),sQuery(id+"F0.wireOp",EDGE,"E20.filletArc"),sQuery(id+"F0.wireOp",EDGE,"E25.0"),sQuery(id+"F0.wireOp",EDGE,"E25.1"),sQuery(id+"F0.wireOp",EDGE,"E25.2"),sQuery(id+"F0.wireOp",EDGE,"E25.3"),sQuery(id+"F0.wireOp",EDGE,"E25.4"),sQuery(id+"F0.wireOp",EDGE,"E25.5"),sQuery(id+"F0.wireOp",EDGE,"E25.6"),sQuery(id+"F0.wireOp",EDGE,"E25.7")])],"isStart":false});
            extrude(context, id + "F17", {"entities" : qUnion([Q0, Q1, Q2]), "operationType" : NewBodyOperationType.ADD, "endBound" : BoundingType.UP_TO_SURFACE, "endBoundEntityFace" : qUnion([Q3]), "depth" : 25 * mm});
        }
    });
